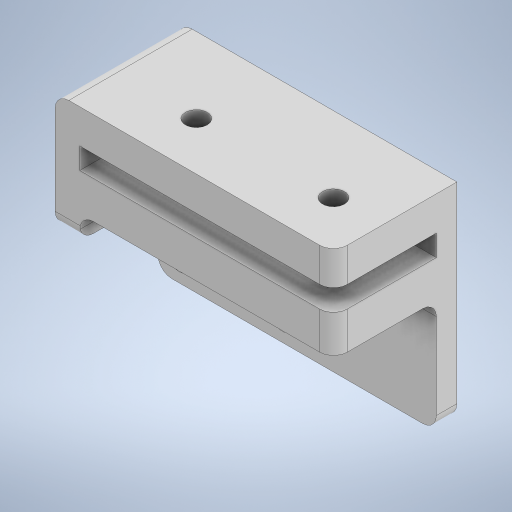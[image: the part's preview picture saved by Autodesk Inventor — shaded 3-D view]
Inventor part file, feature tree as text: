
AUTODESK INVENTOR PART (.ipt)
format: ipt  version: 2024.3 (Build 283343000, 343)  size: 341,504 bytes
history: native  units: mm
features: sketch x7, extrude x5, hole x2, fillet x2, other x1, projected_geometry x1
ambient origin geometry x8: Origin, YZ Plane, XZ Plane, XY Plane, X Axis, Y Axis, Z Axis, Center Point
bodies: Body1 (feature_tree)
feature tree (18):
  other  "ソリッド1"
  extrude  "押し出し1"  Depth=40.0mm
  extrude  "押し出し2"  Depth=30.0mm
  hole  "穴1"  [1 undecoded]
  extrude  "押し出し4"  Depth=3.0mm
  extrude  "押し出し5"  Depth=15.0mm TaperAngle=0.0deg
  extrude  "押し出し7"  Depth=3.0mm
  fillet  "フィレット1"  Radius=3.0mm
  fillet  "フィレット2"  Radius=15.0mm
  hole  "穴3"  [1 undecoded]
  sketch  "スケッチ1"
  sketch  "スケッチ2"
  sketch  "スケッチ5"
  sketch  "スケッチ8"
  sketch  "スケッチ9"
  projected_geometry  "投影ループ1"
  sketch  "スケッチ12"
  sketch  "スケッチ14"
note: 2 required parameter values undecoded (feature->parameter linkage not recoverable at this tier; creation-order binding heuristic only, values carry confidence <= 0.55)
